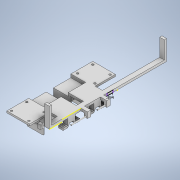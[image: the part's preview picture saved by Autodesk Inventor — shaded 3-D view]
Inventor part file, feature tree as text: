
AUTODESK INVENTOR PART (.ipt)
format: ipt  version: 2020.2 (Build 242310000, 310)  size: 701,952 bytes
history: native  units: mm
features: sketch x36, extrude x35, projected_geometry x10, hole x3
ambient origin geometry x8: Origin, YZ Plane, XZ Plane, XY Plane, X Axis, Y Axis, Z Axis, Center Point
bodies: Solid1 (feature_tree)
feature tree (84):
  sketch  "Sketch1"  dims[d0=8.0mm d1=112.8014mm]
  extrude  "Extrusion1"  Depth=112.8014mm
  extrude  "Extrusion2"  Depth=4.0mm
  extrude  "Extrusion3"  Depth=4.0mm TaperAngle=0.0deg
  extrude  "Extrusion4"  Depth=34.0mm
  extrude  "Extrusion5"  Depth=12.7mm
  extrude  "Extrusion6"  Depth=25.0mm
  hole  "Hole1"  [1 undecoded]
  extrude  "Extrusion11"  TaperAngle=60.0deg  [1 undecoded]
  extrude  "Extrusion12"  TaperAngle=120.0deg  [1 undecoded]
  sketch  "Sketch16"  dims[d19=6.4262mm d20=120.0deg]
  extrude  "Extrusion13"  Depth=6.4262mm
  extrude  "Extrusion14"  Depth=6.4262mm
  sketch  "Sketch17"  dims[d21=120.0deg d22=6.4262mm]
  extrude  "Extrusion15"  Depth=25.4mm TaperAngle=0.0deg
  extrude  "Extrusion18"  Depth=6.0mm
  extrude  "Extrusion19"  Depth=8.89mm
  extrude  "Extrusion20"  Depth=10.0mm
  hole  "Hole2"  [1 undecoded]
  extrude  "Extrusion21"  Depth=2.0mm
  extrude  "Extrusion22"  Depth=2.0mm
  sketch  "Sketch27"  dims[d45=8.89mm d46=2.0mm]
  extrude  "Extrusion23"  Depth=25.4mm
  extrude  "Extrusion24"  Depth=32.48mm
  extrude  "Extrusion25"  TaperAngle=90.0deg  [1 undecoded]
  sketch  "Sketch29"  dims[d79=51.53mm d80=32.48mm]
  extrude  "Extrusion26"  Depth=2.0mm
  extrude  "Extrusion27"  Depth=29.0mm
  extrude  "Extrusion28"  Depth=36.0mm TaperAngle=0.0deg
  sketch  "Sketch31"  dims[d83=4.0mm d84=0.0mm d87=2.0mm]
  extrude  "Extrusion29"  Depth=8.0mm
  extrude  "Extrusion30"  Depth=17.5mm
  extrude  "Extrusion31"  Depth=35.0mm
  extrude  "Extrusion32"  Depth=5.0mm
  extrude  "Extrusion33"  TaperAngle=90.0deg  [1 undecoded]
  extrude  "Extrusion34"  Depth=5.0mm
  extrude  "Extrusion35"  Depth=25.4mm TaperAngle=0.0deg
  extrude  "Extrusion37"  Depth=1.0mm
  extrude  "Extrusion38"  TaperAngle=0.0deg  [1 undecoded]
  extrude  "Extrusion39"  Depth=28.8036mm
  extrude  "Extrusion40"  Depth=25.4mm
  hole  "Hole4"  [1 undecoded]
  extrude  "Extrusion41"  Depth=25.4mm
  extrude  "Extrusion42"  Depth=6.4262mm
  sketch  "Sketch2"  dims[d2=8.0mm d3=4.0mm]
  sketch  "Sketch3"  dims[d4=4.0mm d5=4.0mm d6=0.0mm]
  sketch  "Sketch4"  dims[d7=34.0mm d8=0.0mm d9=19.558mm]
  sketch  "Sketch5"  dims[d10=16.1125mm d11=12.7mm]
  sketch  "Sketch6"  dims[d12=25.0mm d13=0.0mm d14=11.1125mm]
  sketch  "Sketch14"  dims[d15=6.4135mm d16=12.827mm]
  projected_geometry  "Projected Loop2"
  sketch  "Sketch15"  dims[d17=6.4262mm d18=60.0deg]
  projected_geometry  "Projected Loop3"
  sketch  "Sketch18"  dims[d23=120.0deg d24=6.4262mm]
  sketch  "Sketch21"  dims[d25=120.0deg d26=25.4mm d27=0.0mm]
  sketch  "Sketch22"  dims[d28=6.0mm d29=8.89mm]
  sketch  "Sketch23"  dims[d30=5.9944mm d31=8.89mm]
  sketch  "Sketch24"  dims[d32=25.4mm d33=0.0mm d34=10.0mm]
  sketch  "Sketch25"  dims[d35=90.0deg d36=20.0mm]
  projected_geometry  "Projected Loop5"
  sketch  "Sketch26"  dims[d37=3.4mm d38=19.05mm d39=6.2992mm d40=6.35mm d41=90.0deg d42=5.0mm d43=0.0mm d44=2.0mm]
  sketch  "Sketch28"  dims[d47=25.4mm d48=0.0mm d78=16.24mm]
  sketch  "Sketch30"  dims[d81=90.0deg d82=90.0deg]
  sketch  "Sketch32"  dims[d88=2.0mm d89=29.0mm]
  projected_geometry  "Projected Loop6"
  sketch  "Sketch33"  dims[d90=2.0mm d91=36.0mm d92=0.0mm]
  projected_geometry  "Projected Loop7"
  sketch  "Sketch34"  dims[d93=13.878mm d94=8.0mm]
  sketch  "Sketch35"  dims[d95=180.0deg d96=17.5mm]
  projected_geometry  "Projected Loop8"
  sketch  "Sketch36"  dims[d97=90.0deg d98=35.0mm]
  sketch  "Sketch37"  dims[d99=3.5mm d100=5.0mm]
  sketch  "Sketch38"  dims[d101=7.0mm d102=90.0deg]
  sketch  "Sketch41"  dims[d103=5.0mm d104=3.4mm]
  sketch  "Sketch42"  dims[d105=3.4mm d106=25.4mm d107=0.0mm]
  sketch  "Sketch43"  dims[d108=6.4262mm d109=0.0mm d110=1.0mm]
  projected_geometry  "Projected Loop9"
  projected_geometry  "Projected Loop10"
  projected_geometry  "Projected Loop11"
  projected_geometry  "Projected Loop12"
  sketch  "Sketch44"  dims[d111=1.0mm d112=0.0mm d113=0.0mm]
  sketch  "Sketch45"  dims[d128=44.8mm d129=28.8036mm]
  sketch  "Sketch46"  dims[d130=25.4mm d131=0.0mm d132=3.2131mm]
  sketch  "Sketch47"  dims[d133=6.4262mm d134=120.0deg d135=3.2131mm d136=6.4262mm d137=120.0deg d138=25.4mm d139=0.0mm d140=8.001mm d141=13.8938mm d142=8.001mm d143=0.0mm d144=25.4mm d145=0.0mm d146=10.0mm d147=20.0mm d148=3.4mm d149=19.05mm d150=6.2992mm d151=6.35mm d152=90.0deg d153=5.0mm d154=0.0mm d155=16.2433mm d156=32.4866mm d157=51.5366mm d158=4.0mm d159=0.0mm d160=29.0068mm d161=2.0mm d162=2.0mm d163=2.0mm d164=2.0mm d165=36.0mm d166=0.0mm d167=7.0mm d168=5.0mm d169=5.0mm d170=17.5mm d171=35.0mm d172=3.4mm d173=3.4mm d174=5.0mm d175=0.0mm d176=5.0mm d177=0.0mm d178=1.0mm d179=1.0mm d180=25.4mm d181=0.0mm d182=19.05mm d183=10.0mm d184=5.08mm d185=4.0mm d186=0.0mm d187=10.0mm d188=0.0mm d189=2.0mm d190=2.0mm d191=25.4mm d192=0.0mm d193=10.0mm d194=30.0mm d195=0.0mm d196=80.5688mm d197=0.0mm d198=4.0mm d199=30.0mm d200=0.0mm d201=11.43mm d202=0.0mm d203=25.4mm d204=0.0mm d205=25.4mm d206=0.0mm d207=25.4mm d208=0.0mm d237=25.4mm d238=0.0mm d239=25.4mm d240=0.0mm d241=1.5mm d242=0.0mm d243=39.0mm d244=35.0mm d245=39.0mm d246=35.0mm d247=3.0mm d248=0.0mm d249=5.0mm d250=5.0mm d251=29.7mm d252=26.05mm d253=4.0mm d254=4.0mm d255=29.7mm d256=26.05mm d257=3.4mm d258=19.05mm d259=6.2992mm d260=6.35mm d261=90.0deg d262=25.4mm d263=20.594885mm d264=7.8mm d265=0.0mm d266=30.0mm d267=5.7mm d268=29.9974mm d269=25.4mm d270=0.0mm d214=12.7mm d215=0.872665mm d216=12.7mm d217=0.872665mm d228=12.7mm d229=0.872665mm d230=12.7mm d231=0.872665mm]
note: 8 required parameter values undecoded (feature->parameter linkage not recoverable at this tier; creation-order binding heuristic only, values carry confidence <= 0.55)
